# Revit family: Sanitary_Shower-Screens_Sanindusa_New-WCCare-Hinged-Shower-Door
name_source: partatom
category: Plumbing Fixtures
revit_build: Autodesk Revit 2018 (Build: 20170223_1515(x64)
units: mm (PartAtom-declared; Revit-internal decimal feet)

## family parameters
Always vertical = Yes
Cut with Voids When Loaded = No
OmniClass Number = 23.45.00.00
OmniClass Title = Sanitary, Laundry, and Cleaning Equipment
Part Type = Normal
Room Calculation Point = No
Round Connector Dimension = Use Diameter
Shared = No
Work Plane-Based = No

## types (1)
- Sanitary_Shower-Screens_Sanindusa_New-WCCare-Hinged-Shower-Door
    AssetType = Fixed
    Color = Silver
    Constituents = Aluminum profile adjustable; Magnetic closure; 6 mm toughened safety glass; Silicone sealants; Fixing kit and assembly instruction.
150 mm PVC flexible hose; ABS shower bracket, with adjustable height; Fixing Kit.
    Cost = 0 $
    Description = Hinged shower door enclosure new wccare 90 (h185)
    Edition number = 1
    Element Type = SHOWER ENCLOSURES
    Features = Reversible door with lifting mechanism during opening and lowering during closing. Possibility of opening in the upper part. 
For use as a grab bar and a fixed support bar for WCs, showers or washbasins. 
Generally installed parallel to a drop-down bar in a WC or on either side of a washbasin. 
Recommended if the WC pan or shower seat is a long way from the side wall. 
In the lowered position use as a grab bar, for standing up and assisting movement. For WCs or showers. Allows side access in the raised position.
Slowed down descent. Retained in upright position.
Stainless steel  for easy maintenance and hygiene.
    Finish = Bright Silver finish
    Installation Instructions = https://www.tec.sanindusa.pt
    InstallationDate = 1900-12-31T23:59:59
    Manufacturer = Sanindusa
    ManufacturerName = Sanindusa
    ManufacturerURL = www.tec.sanindusa.pt
    Material = Tempered glass, Aluminum
    ModelNumber = 8919200011
    ModelReference = Wccare
    Name = Hinged shower door new wccare
    NominalHeight = 1850 mm  [stored 6.06955 ft]
    NominalLength = 860 mm
    NominalWidth = 0 mm  [stored 0 ft]
    Pre-defined type (IFC) = FURNISHING ELEMENT
    Product Guid = 42100071-6d79-4254-bd5a-903259ad443b
    Product data url = https://bimobject.com
    ProductInformation = https://www.tec.sanindusa.pt
    ProductionYear = 2017
    Size = 86x185
    Type (IFC) = IfcFurnitureType
    URL = www.tec.sanindusa.pt
    Uniclass2015Code = Pr_40_20_06_80
    Uniclass2015Title = Shower enclosures
    Uniclass2015Version = Products v1.7
    Version = 2
    WarrantyDescription = https://www.tec.sanindusa.pt
The warranty will come into force from the moment the warranty detachable bulletin that accompanies the product is received at Sanindusa or from the moment the product is sold to the distributer
Only if the customer issues a writen and justified (Country laws, state laws, commercial strategy) request to Sanindusa, may the above mentioned warranties be the object of a possible change.
    WarrantyDurationParts = 2
    WarrantyDurationUnit = year
    WarrantyStartDate = 1900-12-31T23:59:59
1900-12-31T23:59:59
    Weight = 26.65 kg

note: [stored X ft] marks values corroborated as IEEE doubles in the binary element streams (Revit-internal decimal feet)

## geometry (parser evidence)
native form markers: Sweep x5
no freeform markers — native parametric forms only
